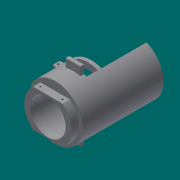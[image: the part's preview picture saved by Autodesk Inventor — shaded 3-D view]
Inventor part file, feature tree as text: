
AUTODESK INVENTOR PART (.ipt)
format: ipt  version: 2013 (Build 170138000, 138)  size: 288,256 bytes
history: native  units: mm
features: extrude x11, sketch x11, other x4, revolve x1, mirror x1, fillet x1
ambient origin geometry x8: Origin, YZ Plane, XZ Plane, XY Plane, X Axis, Y Axis, Z Axis, Center Point
feature tree (29):
  other  "ソリッド1"
  revolve  "回転1"
  other  "作業平面4"
  extrude  "押し出し1"  Depth=32.0mm
  extrude  "押し出し2"  Depth=30.0mm
  extrude  "押し出し3"  Depth=35.0mm
  extrude  "押し出し4"  Depth=2.0mm
  extrude  "押し出し5"  Depth=80.0mm
  mirror  "ミラー1"
  other  "作業平面5"
  extrude  "押し出し7"  TaperAngle=90.0deg  [1 undecoded]
  other  "作業平面6"
  extrude  "押し出し8"  Depth=37.0mm
  extrude  "押し出し9"  Depth=66.0mm
  extrude  "押し出し10"  Depth=46.0mm
  fillet  "フィレット1"  Radius=27.0mm
  extrude  "押し出し11"  Depth=10.0mm
  extrude  "押し出し12"  Depth=40.0mm
  sketch  "スケッチ1"
  sketch  "スケッチ4"
  sketch  "スケッチ5"
  sketch  "スケッチ6"
  sketch  "スケッチ7"
  sketch  "スケッチ8"
  sketch  "スケッチ9"
  sketch  "スケッチ10"
  sketch  "スケッチ11"
  sketch  "スケッチ12"
  sketch  "スケッチ13"
note: 1 required parameter value undecoded (feature->parameter linkage not recoverable at this tier; creation-order binding heuristic only, values carry confidence <= 0.55)
